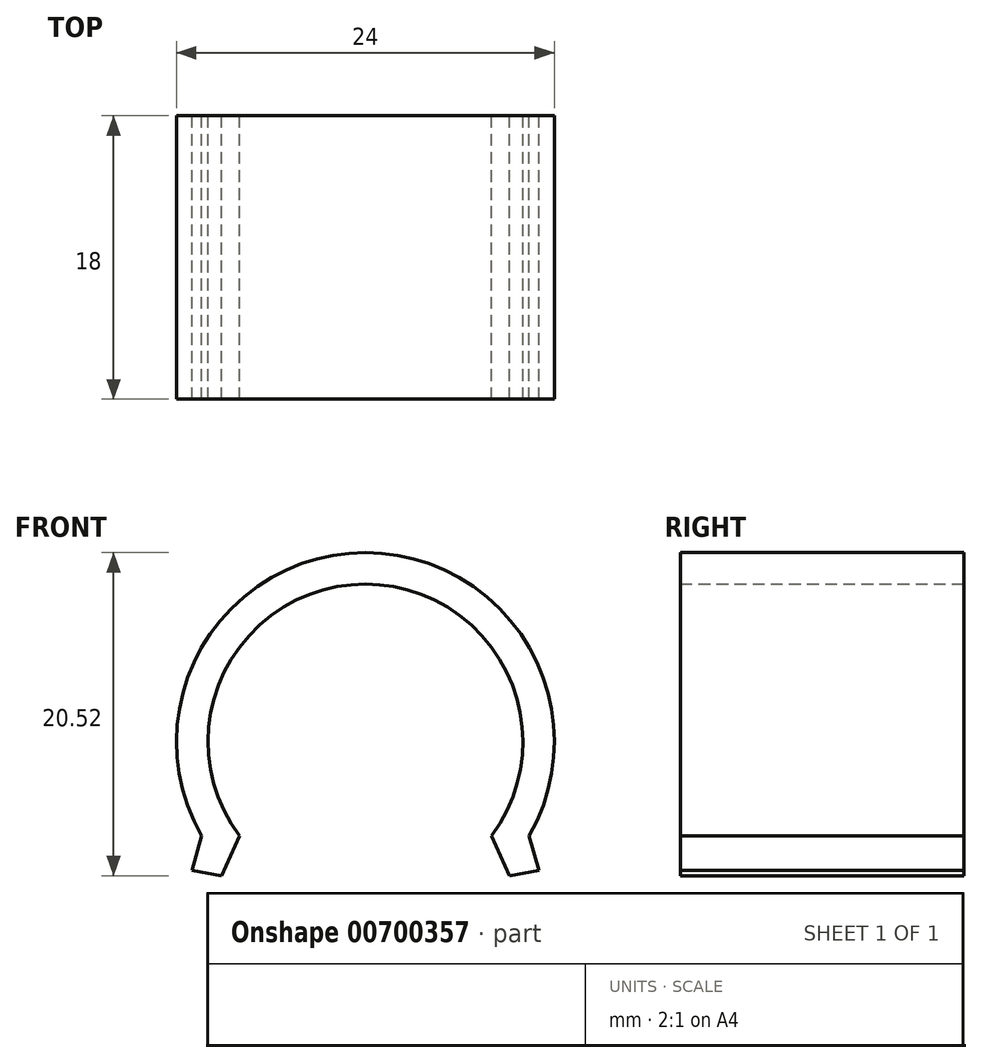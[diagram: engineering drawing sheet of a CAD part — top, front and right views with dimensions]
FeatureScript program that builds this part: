
annotation { "Feature Type Name" : "Feature", "Feature Type Description" : "" }
export const myFeature = defineFeature(function(context is Context, id is Id, definition is map)
    precondition{}
    {
        {
            var Q0;
            Q0=qCreatedBy(makeId("Front.planeOp"),FACE);
            var sketch = newSketch(context, id + "F0", { "sketchPlane" : qUnion([Q0])});
            skArc(sketch, "E0", {"start": v(8, -6) * mm, "mid": v(0, 10) * mm, "end": v(-8, -6) * mm});
            skLineSegment(sketch, "E1", {"start": v(0, 0) * mm, "end": v(0, -23.18) * mm, "construction": true});
            skLineSegment(sketch, "E2", {"start": v(-16.12, -6) * mm, "end": v(17.9, -6) * mm, "construction": true});
            skLineSegment(sketch, "E3", {"start": v(-8, -6) * mm, "end": v(-9.15, -8.52) * mm});
            skArc(sketch, "E4.0", {"start": v(10.4, -6) * mm, "mid": v(0, 12) * mm, "end": v(-10.4, -6) * mm});
            skLineSegment(sketch, "E5.MirrorCS", {"start": v(8, -6) * mm, "end": v(9.15, -8.52) * mm});
            skLineSegment(sketch, "E6", {"start": v(-10.4, -6) * mm, "end": v(-11.02, -8.18) * mm});
            skLineSegment(sketch, "E7", {"start": v(-11.02, -8.18) * mm, "end": v(-9.15, -8.52) * mm});
            skLineSegment(sketch, "E8.MirrorCS", {"start": v(11.02, -8.18) * mm, "end": v(9.15, -8.52) * mm});
            skLineSegment(sketch, "E9.MirrorCS", {"start": v(10.4, -6) * mm, "end": v(11.02, -8.18) * mm});
            skSolve(sketch);
        }
        {
            var Q0;
            Q0=makeQuery(id+"F0.imprint","IMPRINT",FACE,{"disambiguationData":[TD([[makeQuery(id+"F0.imprint","IMPRINT",EDGE,{"derivedFrom":sQuery(id+"F0.wireOp",EDGE,"E0")}),-1.0]])]});
            extrude(context, id + "F1", {"entities" : qUnion([Q0]), "depth" : 18 * mm, "offsetDistance" : 25 * mm});
        }
    });
